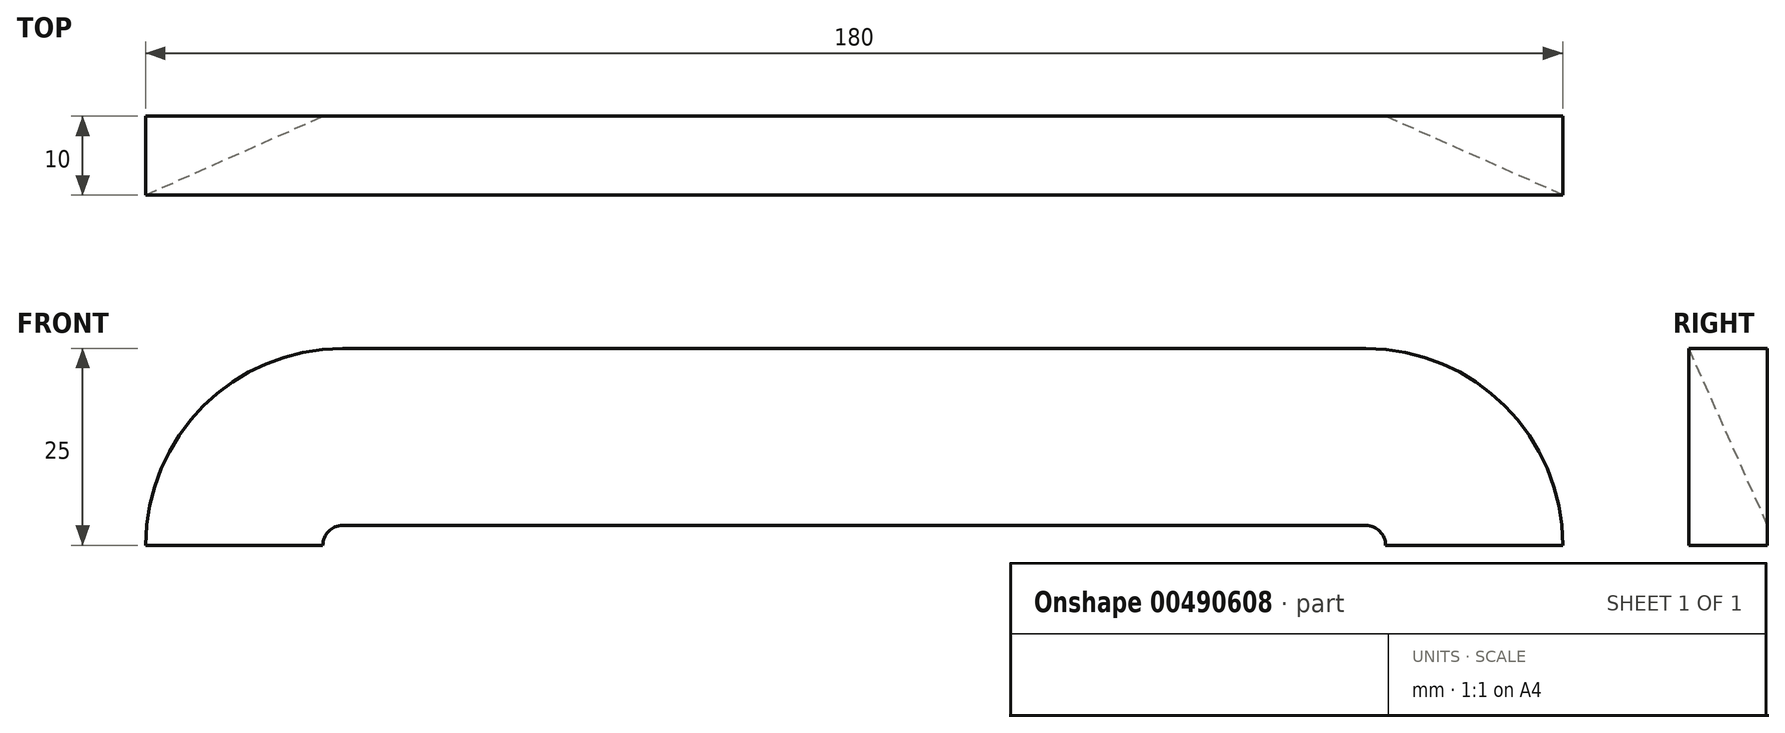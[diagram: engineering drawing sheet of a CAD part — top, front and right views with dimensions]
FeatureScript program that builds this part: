
annotation { "Feature Type Name" : "Feature", "Feature Type Description" : "" }
export const myFeature = defineFeature(function(context is Context, id is Id, definition is map)
    precondition{}
    {
        {
            var Q0;
            Q0=qCreatedBy(makeId("Top.planeOp"),FACE);
            var sketch = newSketch(context, id + "F0", { "sketchPlane" : qUnion([Q0])});
            skLineSegment(sketch, "E0", {"start": v(-90, 0) * mm, "end": v(90, 0) * mm});
            skSolve(sketch);
        }
        {
            var Q0;
            Q0=qCreatedBy(makeId("Top.planeOp"),FACE);
            var sketch = newSketch(context, id + "F1", { "sketchPlane" : qUnion([Q0])});
            skLineSegment(sketch, "E1", {"start": v(90, 0) * mm, "end": v(67.5, 0) * mm});
            skLineSegment(sketch, "E2", {"start": v(90, 0) * mm, "end": v(90, -10) * mm});
            skLineSegment(sketch, "E3", {"start": v(90, -10) * mm, "end": v(67.5, 0) * mm});
            skLineSegment(sketch, "E4", {"start": v(65, 56.08) * mm, "end": v(65, -29.56) * mm});
            skSolve(sketch);
        }
        {
            var Q0;
            Q0=makeQuery(id+"F1.imprint","IMPRINT",FACE,{"disambiguationData":[TD([[makeQuery(id+"F1.imprint","IMPRINT",EDGE,{"derivedFrom":sQuery(id+"F1.wireOp",EDGE,"E1")}),1.0]])]});
            var Q1;
            Q1=sQuery(id+"F1.wireOp",EDGE,"E4");
            revolve(context, id + "F2", {"entities" : qUnion([Q0]), "axis" : qUnion([Q1]), "revolveType" : RevolveType.ONE_DIRECTION, "angle" : 90 * degree});
        }
        {
            var Q0;
            Q0=makeQuery(id+"F2.opRevolve","CAP_FACE",FACE,{"disambiguationData":[OSD([sQuery(id+"F1.wireOp",EDGE,"E1"),sQuery(id+"F1.wireOp",EDGE,"E2"),sQuery(id+"F1.wireOp",EDGE,"E3")])],"isStart":false});
            extrude(context, id + "F3", {"entities" : qUnion([Q0]), "operationType" : NewBodyOperationType.ADD, "depth" : 65 * mm});
        }
        {
            var Q0;
            Q0=makeQuery(id+"F2.opRevolve","SWEPT_BODY",BODY,{"disambiguationData":[OSD([sQuery(id+"F1.wireOp",EDGE,"E1"),sQuery(id+"F1.wireOp",EDGE,"E2"),sQuery(id+"F1.wireOp",EDGE,"E3")])]});
            var Q1;
            Q1=qCreatedBy(makeId("Right.planeOp"),FACE);
            mirror(context, id + "F4", {"operationType" : NewBodyOperationType.ADD, "entities" : qUnion([Q0]), "mirrorPlane" : qUnion([Q1])});
        }
    });
